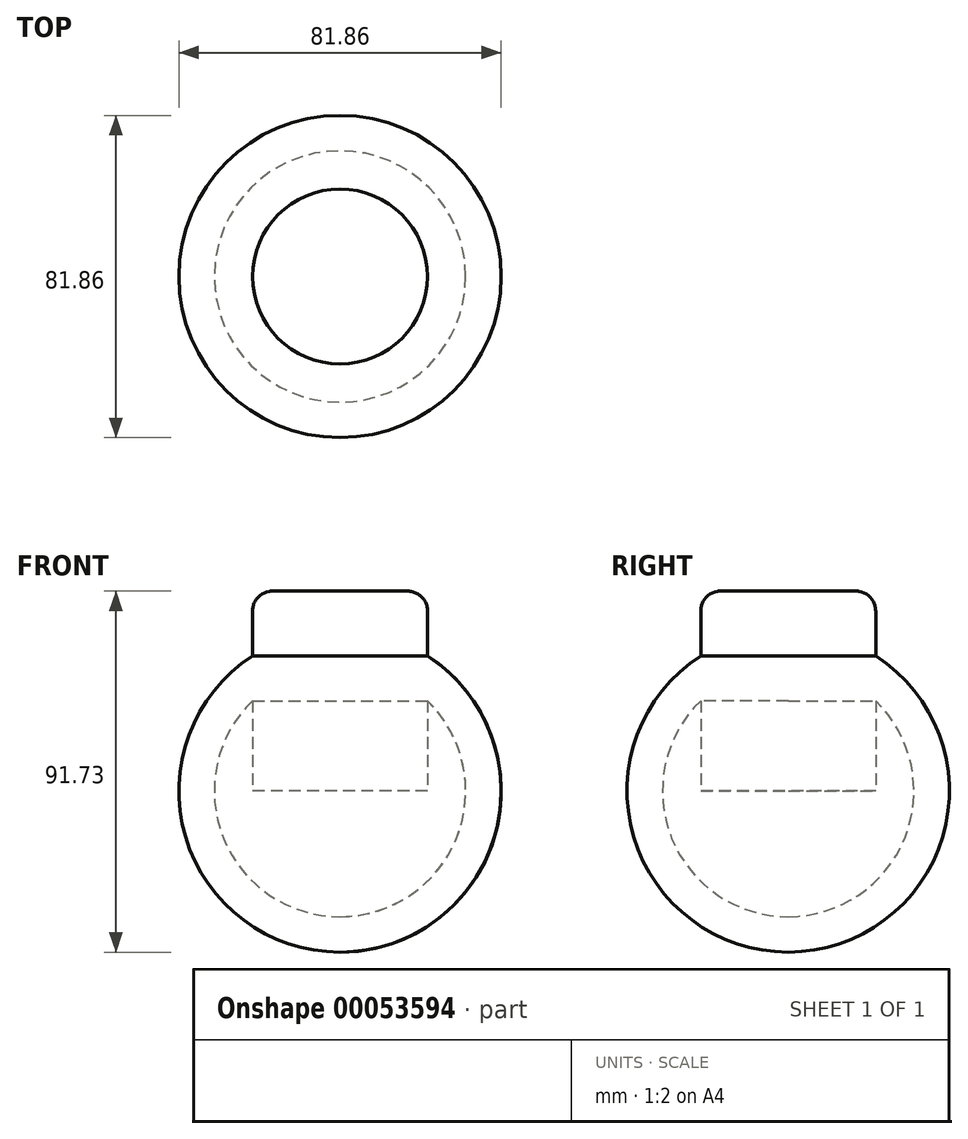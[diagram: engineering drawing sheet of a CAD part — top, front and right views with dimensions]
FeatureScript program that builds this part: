
annotation { "Feature Type Name" : "Feature", "Feature Type Description" : "" }
export const myFeature = defineFeature(function(context is Context, id is Id, definition is map)
    precondition{}
    {
        {
            var Q0;
            Q0=qCreatedBy(makeId("Front.planeOp"),FACE);
            var sketch = newSketch(context, id + "F0", { "sketchPlane" : qUnion([Q0])});
            skArc(sketch, "E0", {"start": v(0, -40.93) * mm, "mid": v(40.93, 0) * mm, "end": v(0, 40.93) * mm});
            skLineSegment(sketch, "E1", {"start": v(0, 40.93) * mm, "end": v(0, -40.93) * mm});
            skLineSegment(sketch, "E2", {"start": v(31.93, 0) * mm, "end": v(-31.93, 0) * mm});
            skLineSegment(sketch, "E3", {"start": v(-31.93, 0) * mm, "end": v(0, 0) * mm});
            skLineSegment(sketch, "E4", {"start": v(31.93, 0) * mm, "end": v(0, 0) * mm});
            skCircle(sketch, "E5", {"center": v(0, 0) * mm, "radius": 31.93 * mm});
            skLineSegment(sketch, "E6", {"start": v(40.93, 0) * mm, "end": v(-40.93, 0) * mm});
            skPoint(sketch, "E6.endSnap0", {"position": v(-15.97, 0) * mm});
            skArc(sketch, "E7", {"start": v(0, 40.93) * mm, "mid": v(-40.93, 0) * mm, "end": v(0, -40.93) * mm});
            skSolve(sketch);
        }
        {
            var Q0;
            Q0=makeQuery(id+"F0.imprint","IMPRINT",FACE,{"disambiguationData":[TD([[makeQuery(id+"F0.imprint","IMPRINT",EDGE,{"derivedFrom":sQuery(id+"F0.wireOp",EDGE,"E0")}),1.0]])]});
            var Q1;
            Q1=sQuery(id+"F0.wireOp",EDGE,"E1");
            revolve(context, id + "F1", {"entities" : qUnion([Q0]), "axis" : qUnion([Q1]), "revolveType" : RevolveType.FULL});
        }
        {
            var Q0;
            Q0=qCreatedBy(makeId("Top.planeOp"),FACE);
            var sketch = newSketch(context, id + "F2", { "sketchPlane" : qUnion([Q0])});
            skCircle(sketch, "E8", {"center": v(0, 0) * mm, "radius": 22.23 * mm});
            skSolve(sketch);
        }
        {
            var Q0;
            Q0 = qSketchRegion(id + "F2", true);
            extrude(context, id + "F3", {"entities" : qUnion([Q0]), "operationType" : NewBodyOperationType.ADD, "depth" : 50.8 * mm});
        }
        {
            var Q0;
            Q0=makeQuery(id+"F3.opExtrude","CAP_EDGE",EDGE,{"disambiguationData":[OSD([sQuery(id+"F2.wireOp",EDGE,"E8")])],"isStart":false});
            fillet(context, id + "F4", {"entities" : qUnion([Q0]), "radius" : 5.08 * mm, "tangentPropagation" : true, "allowEdgeOverflow" : false});
        }
    });
